SOLIDWORKS PART (.sldprt)
format: sldprt  version: not decoded by parser v0  size: 64,512 bytes
history: native  units: mm
features: sketch x4, plane x3, extrude x2, revolve x1 (+7 scaffold rows collapsed)
feature tree (17):
  scaffold x7  (default folders/planes/origin — collapsed)
  plane  "front x-y"
  plane  "top y-z"
  plane  "side x-z"
  sketch  "Sketch1"  dims[c1.D5=50.8mm c1.D6=12.7mm c1.D1=228.6mm c1.D2=114.3mm c1.D3=76.2mm c1.D4=6.35mm c1.D7=~113.592253mm c2.D7=135.0deg]
  extrude  "Base-Extrude"  Depth=25.4mm
  sketch  "Sketch2"  dims[D1=25.4mm D2=25.4mm]
  extrude  "Boss-Extrude1"  Depth=50.8mm
  sketch  "Sketch3"
  sketch  "Sketch4"  dims[D1=25.4mm]
  revolve  "Boss-Revolve1"  Angle=180deg
decode coverage: 6 of 7 modeling features carry decoded parameters
note: ~ marks probable driven/reference dimensions
note: suppression state not decoded; provenance and decode notes live in map.json
